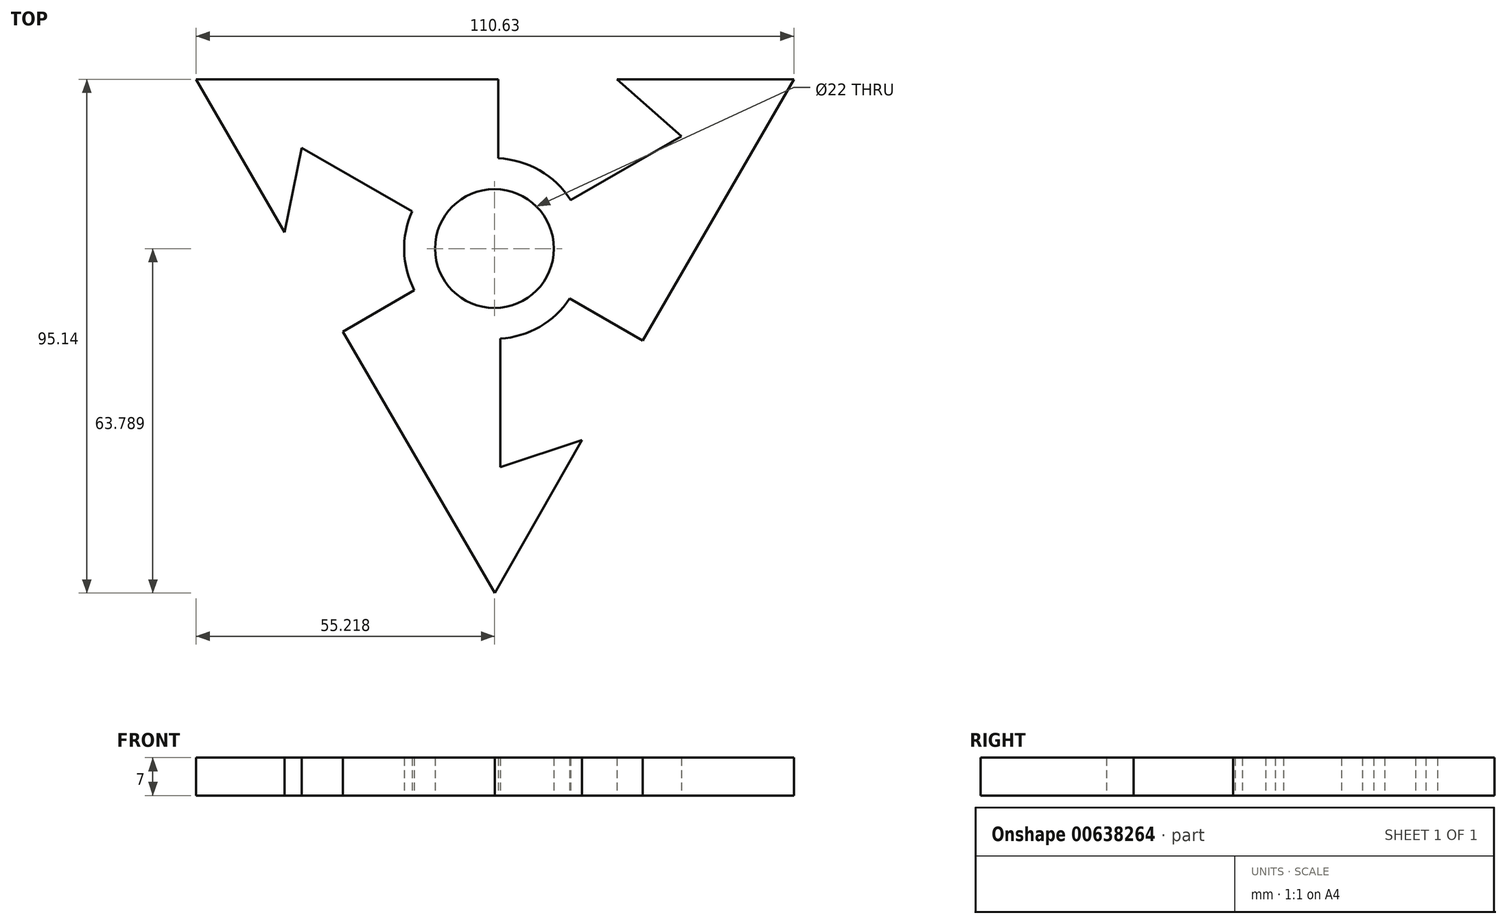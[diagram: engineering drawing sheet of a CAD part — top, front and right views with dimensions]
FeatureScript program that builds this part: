
annotation { "Feature Type Name" : "Feature", "Feature Type Description" : "" }
export const myFeature = defineFeature(function(context is Context, id is Id, definition is map)
    precondition{}
    {
        {
            var Q0;
            Q0=qCreatedBy(makeId("Top.planeOp"),FACE);
            var sketch = newSketch(context, id + "F0", { "sketchPlane" : qUnion([Q0])});
            skCircle(sketch, "E0", {"center": v(-80.16, 63.79) * mm, "radius": 11 * mm});
            skPoint(sketch, "E0.first.point", {"position": v(-80.38, 74.79) * mm});
            skPoint(sketch, "E0.second.point", {"position": v(-79.8, 52.8) * mm});
            skPoint(sketch, "E0.third.point", {"position": v(-69.31, 61.97) * mm});
            skCircle(sketch, "E1", {"center": v(-80.16, 63.79) * mm, "radius": 16.72 * mm});
            skLineSegment(sketch, "E2", {"start": v(-52.72, 46.74) * mm, "end": v(-66.24, 54.52) * mm});
            skLineSegment(sketch, "E3", {"start": v(-52.72, 46.74) * mm, "end": v(-24.75, 95.14) * mm});
            skLineSegment(sketch, "E4", {"start": v(-24.75, 95.14) * mm, "end": v(-57.5, 95.14) * mm});
            skLineSegment(sketch, "E5", {"start": v(-57.5, 95.14) * mm, "end": v(-45.52, 84.59) * mm});
            skLineSegment(sketch, "E6", {"start": v(-45.52, 84.59) * mm, "end": v(-66.06, 72.78) * mm});
            skLineSegment(sketch, "E7", {"start": v(-79.46, 80.5) * mm, "end": v(-79.46, 95.14) * mm});
            skLineSegment(sketch, "E8", {"start": v(-79.46, 95.14) * mm, "end": v(-135.38, 95.14) * mm});
            skLineSegment(sketch, "E9", {"start": v(-135.38, 95.14) * mm, "end": v(-119.03, 66.82) * mm});
            skLineSegment(sketch, "E10", {"start": v(-119.03, 66.82) * mm, "end": v(-115.86, 82.43) * mm});
            skLineSegment(sketch, "E11", {"start": v(-115.86, 82.43) * mm, "end": v(-95.4, 70.67) * mm});
            skLineSegment(sketch, "E12", {"start": v(-79.09, 47.1) * mm, "end": v(-79.09, 23.33) * mm});
            skLineSegment(sketch, "E13", {"start": v(-79.09, 23.33) * mm, "end": v(-63.94, 28.35) * mm});
            skLineSegment(sketch, "E14", {"start": v(-63.94, 28.35) * mm, "end": v(-80.06, 0) * mm});
            skLineSegment(sketch, "E15", {"start": v(-80.06, 0) * mm, "end": v(-108.2, 48.42) * mm});
            skLineSegment(sketch, "E16", {"start": v(-108.2, 48.42) * mm, "end": v(-95, 56.1) * mm});
            skSolve(sketch);
        }
        {
            var Q0;
            {var subQ0=sQuery(id+"F0.wireOp",EDGE,"E12");Q0=makeQuery(id+"F0.imprint","IMPRINT",FACE,{"disambiguationData":[TD([[makeQuery(id+"F0.imprint","IMPRINT",EDGE,{"derivedFrom":subQ0}),-1.0]])]});}
            var Q1;
            Q1=makeQuery(id+"F0.imprint","IMPRINT",FACE,{"disambiguationData":[TD([[makeQuery(id+"F0.imprint","IMPRINT",EDGE,{"derivedFrom":sQuery(id+"F0.wireOp",EDGE,"E0")}),-1.0]])]});
            var Q2;
            {var subQ0=sQuery(id+"F0.wireOp",EDGE,"E7");Q2=makeQuery(id+"F0.imprint","IMPRINT",FACE,{"disambiguationData":[TD([[makeQuery(id+"F0.imprint","IMPRINT",EDGE,{"derivedFrom":subQ0}),1.0]])]});}
            var Q3;
            {var subQ0=sQuery(id+"F0.wireOp",EDGE,"E2");Q3=makeQuery(id+"F0.imprint","IMPRINT",FACE,{"disambiguationData":[TD([[makeQuery(id+"F0.imprint","IMPRINT",EDGE,{"derivedFrom":subQ0}),-1.0]])]});}
            extrude(context, id + "F1", {"entities" : qUnion([Q0, Q1, Q2, Q3]), "depth" : 7 * mm, "offsetDistance" : 25.4 * mm});
        }
    });
